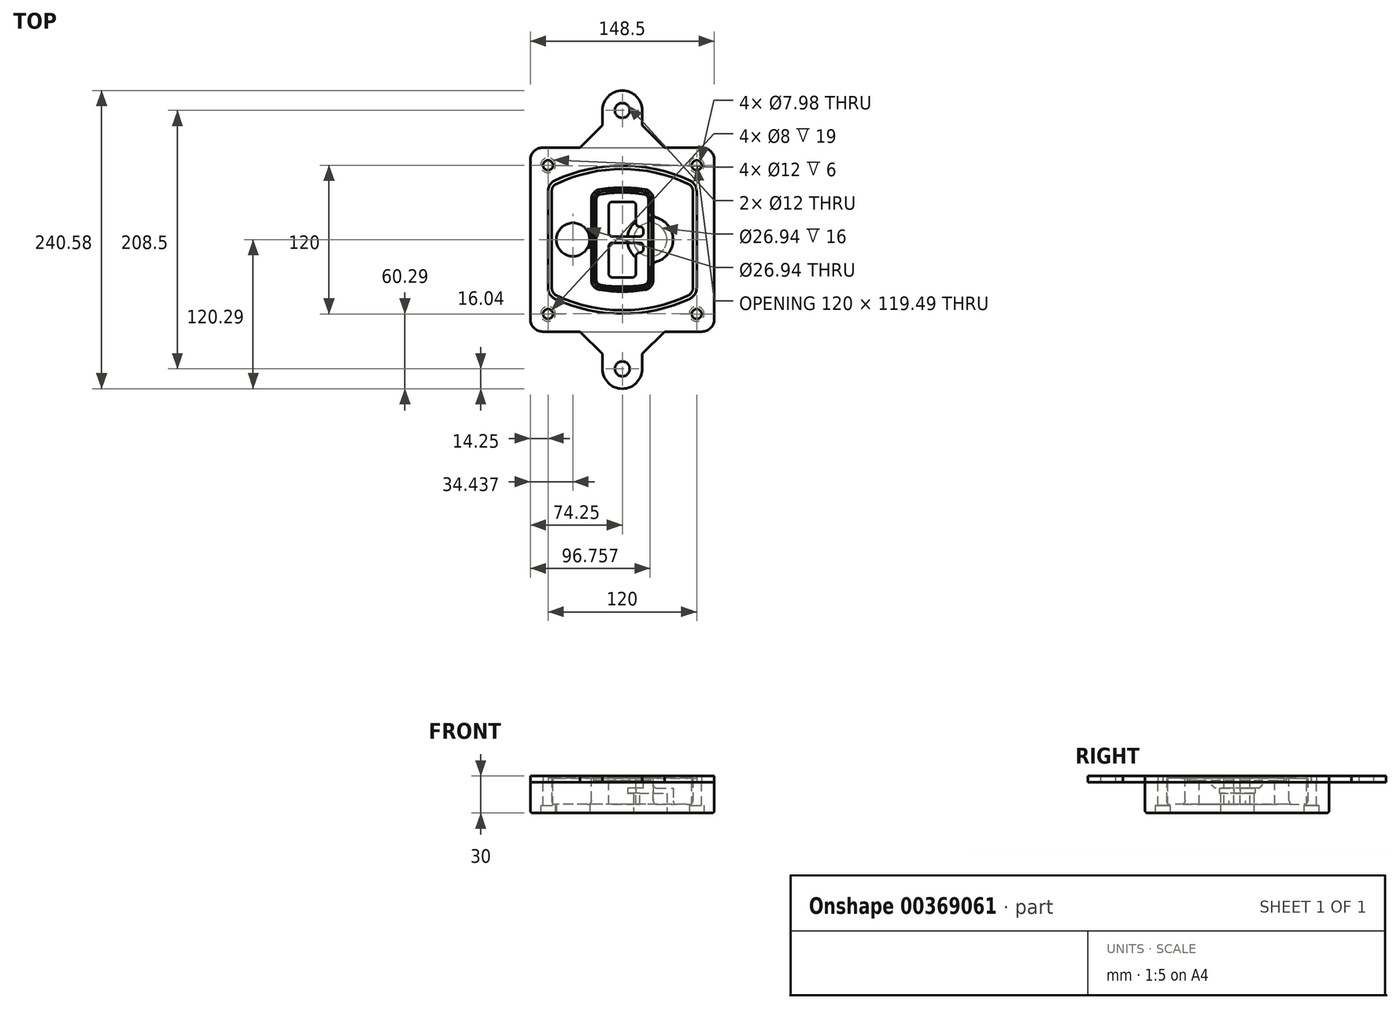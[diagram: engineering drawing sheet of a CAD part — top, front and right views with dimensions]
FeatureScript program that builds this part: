
annotation { "Feature Type Name" : "Feature", "Feature Type Description" : "" }
export const myFeature = defineFeature(function(context is Context, id is Id, definition is map)
    precondition{}
    {
        {
            var Q0;
            Q0=qCreatedBy(makeId("Top.planeOp"),FACE);
            var sketch = newSketch(context, id + "F0", { "sketchPlane" : qUnion([Q0])});
            skPoint(sketch, "E0.rect.middle", {"position": v(0, 0) * mm});
            skLineSegment(sketch, "E1.bottom", {"start": v(-64.25, -74.25) * mm, "end": v(64.25, -74.25) * mm});
            skLineSegment(sketch, "E1.top", {"start": v(-64.25, 74.25) * mm, "end": v(64.25, 74.25) * mm});
            skLineSegment(sketch, "E1.left", {"start": v(-74.25, -64.25) * mm, "end": v(-74.25, 64.25) * mm});
            skLineSegment(sketch, "E1.right", {"start": v(74.25, -64.25) * mm, "end": v(74.25, 64.25) * mm});
            skLineSegment(sketch, "E2", {"start": v(-74.25, 74.25) * mm, "end": v(74.25, -74.25) * mm, "construction": true});
            skLineSegment(sketch, "E3", {"start": v(74.25, 74.25) * mm, "end": v(-74.25, -74.25) * mm, "construction": true});
            skCircle(sketch, "E4", {"center": v(-60, 60) * mm, "radius": 4 * mm});
            skCircle(sketch, "E5", {"center": v(60, 60) * mm, "radius": 4 * mm});
            skCircle(sketch, "E6", {"center": v(60, -60) * mm, "radius": 4 * mm});
            skCircle(sketch, "E7", {"center": v(-60, -60) * mm, "radius": 4 * mm});
            skLineSegment(sketch, "E8", {"start": v(-60, 60) * mm, "end": v(60, 60) * mm, "construction": true});
            skLineSegment(sketch, "E9", {"start": v(60, 60) * mm, "end": v(60, -60) * mm, "construction": true});
            skLineSegment(sketch, "E10", {"start": v(60, -60) * mm, "end": v(-60, -60) * mm, "construction": true});
            skLineSegment(sketch, "E11", {"start": v(-60, -60) * mm, "end": v(-60, 60) * mm, "construction": true});
            skLineSegment(sketch, "E12", {"start": v(-60, 38.83) * mm, "end": v(-60, -38.83) * mm});
            skLineSegment(sketch, "E13", {"start": v(60, 38.83) * mm, "end": v(60, -38.83) * mm});
            skArc(sketch, "E14", {"start": v(54.26, 47.88) * mm, "mid": v(0, 60) * mm, "end": v(-54.26, 47.88) * mm});
            skArc(sketch, "E15", {"start": v(-54.26, -47.88) * mm, "mid": v(0, -60) * mm, "end": v(54.26, -47.88) * mm});
            skLineSegment(sketch, "E16", {"start": v(-60, 0) * mm, "end": v(60, 0) * mm, "construction": true});
            skPoint(sketch, "E17.visualSharp", {"position": v(-60, -45) * mm});
            skArc(sketch, "E17.filletArc", {"start": v(-60, -38.83) * mm, "mid": v(-58.44, -44.2) * mm, "end": v(-54.26, -47.88) * mm});
            skPoint(sketch, "E18.visualSharp", {"position": v(-60, 45) * mm});
            skArc(sketch, "E18.filletArc", {"start": v(-54.26, 47.88) * mm, "mid": v(-58.44, 44.2) * mm, "end": v(-60, 38.83) * mm});
            skPoint(sketch, "E19.visualSharp", {"position": v(60, 45) * mm});
            skArc(sketch, "E19.filletArc", {"start": v(60, 38.83) * mm, "mid": v(58.44, 44.2) * mm, "end": v(54.26, 47.88) * mm});
            skPoint(sketch, "E20.visualSharp", {"position": v(60, -45) * mm});
            skArc(sketch, "E20.filletArc", {"start": v(54.26, -47.88) * mm, "mid": v(58.44, -44.2) * mm, "end": v(60, -38.83) * mm});
            skPoint(sketch, "E21.visualSharp", {"position": v(-74.25, 74.25) * mm});
            skArc(sketch, "E21.filletArc", {"start": v(-64.25, 74.25) * mm, "mid": v(-71.32, 71.32) * mm, "end": v(-74.25, 64.25) * mm});
            skPoint(sketch, "E22.visualSharp", {"position": v(74.25, 74.25) * mm});
            skArc(sketch, "E22.filletArc", {"start": v(74.25, 64.25) * mm, "mid": v(71.32, 71.32) * mm, "end": v(64.25, 74.25) * mm});
            skPoint(sketch, "E23.visualSharp", {"position": v(74.25, -74.25) * mm});
            skArc(sketch, "E23.filletArc", {"start": v(64.25, -74.25) * mm, "mid": v(71.32, -71.32) * mm, "end": v(74.25, -64.25) * mm});
            skPoint(sketch, "E24.visualSharp", {"position": v(-74.25, -74.25) * mm});
            skArc(sketch, "E24.filletArc", {"start": v(-74.25, -64.25) * mm, "mid": v(-71.32, -71.32) * mm, "end": v(-64.25, -74.25) * mm});
            skArc(sketch, "E25.0", {"start": v(57, 38.83) * mm, "mid": v(55.9, 42.58) * mm, "end": v(52.98, 45.17) * mm});
            skLineSegment(sketch, "E25.1", {"start": v(57, 38.83) * mm, "end": v(57, -38.83) * mm});
            skArc(sketch, "E25.2", {"start": v(52.98, -45.17) * mm, "mid": v(55.9, -42.58) * mm, "end": v(57, -38.83) * mm});
            skArc(sketch, "E25.3", {"start": v(-52.98, -45.17) * mm, "mid": v(0, -57) * mm, "end": v(52.98, -45.17) * mm});
            skArc(sketch, "E25.4", {"start": v(-57, -38.83) * mm, "mid": v(-55.9, -42.58) * mm, "end": v(-52.98, -45.17) * mm});
            skArc(sketch, "E25.5", {"start": v(52.98, 45.17) * mm, "mid": v(0, 57) * mm, "end": v(-52.98, 45.17) * mm});
            skLineSegment(sketch, "E25.6", {"start": v(-57, 38.83) * mm, "end": v(-57, -38.83) * mm});
            skArc(sketch, "E25.7", {"start": v(-52.98, 45.17) * mm, "mid": v(-55.9, 42.58) * mm, "end": v(-57, 38.83) * mm});
            skArc(sketch, "E26.0", {"start": v(-55.96, 51.5) * mm, "mid": v(-61.82, 46.33) * mm, "end": v(-64, 38.83) * mm});
            skArc(sketch, "E26.1", {"start": v(55.96, 51.5) * mm, "mid": v(0, 64) * mm, "end": v(-55.96, 51.5) * mm});
            skArc(sketch, "E26.2", {"start": v(64, 38.83) * mm, "mid": v(61.82, 46.33) * mm, "end": v(55.96, 51.5) * mm});
            skLineSegment(sketch, "E26.3", {"start": v(64, 38.83) * mm, "end": v(64, -38.83) * mm});
            skArc(sketch, "E26.4", {"start": v(55.96, -51.5) * mm, "mid": v(61.82, -46.33) * mm, "end": v(64, -38.83) * mm});
            skLineSegment(sketch, "E26.5", {"start": v(-64, 38.83) * mm, "end": v(-64, -38.83) * mm});
            skArc(sketch, "E26.6", {"start": v(-55.96, -51.5) * mm, "mid": v(0, -64) * mm, "end": v(55.96, -51.5) * mm});
            skArc(sketch, "E26.7", {"start": v(-64, -38.83) * mm, "mid": v(-61.82, -46.33) * mm, "end": v(-55.96, -51.5) * mm});
            skSolve(sketch);
        }
        {
            var Q0;
            Q0=makeQuery(id+"F0.imprint","IMPRINT",FACE,{"disambiguationData":[TD([[makeQuery(id+"F0.imprint","IMPRINT",EDGE,{"derivedFrom":sQuery(id+"F0.wireOp",EDGE,"E1.bottom")}),1.0]])]});
            var Q1;
            Q1=makeQuery(id+"F0.imprint","IMPRINT",FACE,{"disambiguationData":[TD([[makeQuery(id+"F0.imprint","IMPRINT",EDGE,{"derivedFrom":sQuery(id+"F0.wireOp",EDGE,"E12")}),1.0]])]});
            var Q2;
            Q2=makeQuery(id+"F0.imprint","IMPRINT",FACE,{"disambiguationData":[TD([[makeQuery(id+"F0.imprint","IMPRINT",EDGE,{"derivedFrom":sQuery(id+"F0.wireOp",EDGE,"E25.0")}),1.0]])]});
            var Q3;
            Q3=makeQuery(id+"F0.imprint","IMPRINT",FACE,{"disambiguationData":[TD([[makeQuery(id+"F0.imprint","IMPRINT",EDGE,{"derivedFrom":sQuery(id+"F0.wireOp",EDGE,"E12")}),-1.0]])]});
            extrude(context, id + "F1", {"entities" : qUnion([Q0, Q1, Q2, Q3]), "oppositeDirection" : true, "depth" : 25 * mm});
        }
        {
            var Q0;
            Q0=makeQuery(id+"F0.imprint","IMPRINT",FACE,{"disambiguationData":[TD([[makeQuery(id+"F0.imprint","IMPRINT",EDGE,{"derivedFrom":sQuery(id+"F0.wireOp",EDGE,"E12")}),1.0]])]});
            extrude(context, id + "F2", {"entities" : qUnion([Q0]), "operationType" : NewBodyOperationType.ADD, "depth" : 3 * mm});
        }
        {
            var Q0;
            Q0=makeQuery(id+"F0.imprint","IMPRINT",FACE,{"disambiguationData":[TD([[makeQuery(id+"F0.imprint","IMPRINT",EDGE,{"derivedFrom":sQuery(id+"F0.wireOp",EDGE,"E25.0")}),1.0]])]});
            extrude(context, id + "F3", {"entities" : qUnion([Q0]), "operationType" : NewBodyOperationType.REMOVE, "oppositeDirection" : true, "depth" : 18 * mm});
        }
        {
            var Q0;
            Q0=makeQuery(id+"F2.opExtrude","CAP_FACE",FACE,{"disambiguationData":[OSD([sQuery(id+"F0.wireOp",EDGE,"E12"),sQuery(id+"F0.wireOp",EDGE,"E13"),sQuery(id+"F0.wireOp",EDGE,"E14"),sQuery(id+"F0.wireOp",EDGE,"E15"),sQuery(id+"F0.wireOp",EDGE,"E17.filletArc"),sQuery(id+"F0.wireOp",EDGE,"E18.filletArc"),sQuery(id+"F0.wireOp",EDGE,"E19.filletArc"),sQuery(id+"F0.wireOp",EDGE,"E20.filletArc"),sQuery(id+"F0.wireOp",EDGE,"E25.0"),sQuery(id+"F0.wireOp",EDGE,"E25.1"),sQuery(id+"F0.wireOp",EDGE,"E25.2"),sQuery(id+"F0.wireOp",EDGE,"E25.3"),sQuery(id+"F0.wireOp",EDGE,"E25.4"),sQuery(id+"F0.wireOp",EDGE,"E25.5"),sQuery(id+"F0.wireOp",EDGE,"E25.6"),sQuery(id+"F0.wireOp",EDGE,"E25.7")])],"isStart":false});
            var sketch = newSketch(context, id + "F4", { "sketchPlane" : qUnion([Q0])});
            skArc(sketch, "E27.0", {"start": v(-18.34, -40.45) * mm, "mid": v(0, -42) * mm, "end": v(18.34, -40.45) * mm});
            skArc(sketch, "E28.0", {"start": v(18.34, 40.45) * mm, "mid": v(0, 42) * mm, "end": v(-18.34, 40.45) * mm});
            skLineSegment(sketch, "E29", {"start": v(-25, 32.57) * mm, "end": v(-25, -32.57) * mm});
            skLineSegment(sketch, "E30", {"start": v(25, 32.57) * mm, "end": v(25, -32.57) * mm});
            skLineSegment(sketch, "E31", {"start": v(-25, 39.1) * mm, "end": v(25, 39.1) * mm, "construction": true});
            skLineSegment(sketch, "E32", {"start": v(-25, -39.1) * mm, "end": v(25, -39.1) * mm, "construction": true});
            skPoint(sketch, "E33.visualSharp", {"position": v(-25, 39.1) * mm});
            skArc(sketch, "E33.filletArc", {"start": v(-18.34, 40.45) * mm, "mid": v(-23.11, 37.73) * mm, "end": v(-25, 32.57) * mm});
            skPoint(sketch, "E34.visualSharp", {"position": v(25, 39.1) * mm});
            skArc(sketch, "E34.filletArc", {"start": v(25, 32.57) * mm, "mid": v(23.11, 37.73) * mm, "end": v(18.34, 40.45) * mm});
            skPoint(sketch, "E35.visualSharp", {"position": v(25, -39.1) * mm});
            skArc(sketch, "E35.filletArc", {"start": v(18.34, -40.45) * mm, "mid": v(23.11, -37.73) * mm, "end": v(25, -32.57) * mm});
            skPoint(sketch, "E36.visualSharp", {"position": v(-25, -39.1) * mm});
            skArc(sketch, "E36.filletArc", {"start": v(-25, -32.57) * mm, "mid": v(-23.11, -37.73) * mm, "end": v(-18.34, -40.45) * mm});
            skArc(sketch, "E37.0", {"start": v(52.98, 45.17) * mm, "mid": v(0, 57) * mm, "end": v(-52.98, 45.17) * mm});
            skArc(sketch, "E37.1", {"start": v(-52.98, 45.17) * mm, "mid": v(-55.9, 42.58) * mm, "end": v(-57, 38.83) * mm});
            skLineSegment(sketch, "E37.2", {"start": v(-57, 38.83) * mm, "end": v(-57, -38.83) * mm});
            skArc(sketch, "E37.3", {"start": v(-57, -38.83) * mm, "mid": v(-55.9, -42.58) * mm, "end": v(-52.98, -45.17) * mm});
            skArc(sketch, "E37.4", {"start": v(-52.98, -45.17) * mm, "mid": v(0, -57) * mm, "end": v(52.98, -45.17) * mm});
            skArc(sketch, "E37.5", {"start": v(52.98, -45.17) * mm, "mid": v(55.9, -42.58) * mm, "end": v(57, -38.83) * mm});
            skLineSegment(sketch, "E37.6", {"start": v(57, 38.83) * mm, "end": v(57, -38.83) * mm});
            skArc(sketch, "E37.7", {"start": v(57, 38.83) * mm, "mid": v(55.9, 42.58) * mm, "end": v(52.98, 45.17) * mm});
            skLineSegment(sketch, "E38.0", {"start": v(23, 32.57) * mm, "end": v(23, -32.57) * mm});
            skArc(sketch, "E38.1", {"start": v(18, -38.48) * mm, "mid": v(21.58, -36.44) * mm, "end": v(23, -32.57) * mm});
            skArc(sketch, "E38.2", {"start": v(-18, -38.48) * mm, "mid": v(0, -40) * mm, "end": v(18, -38.48) * mm});
            skArc(sketch, "E38.3", {"start": v(-23, -32.57) * mm, "mid": v(-21.58, -36.44) * mm, "end": v(-18, -38.48) * mm});
            skLineSegment(sketch, "E38.4", {"start": v(-23, 32.57) * mm, "end": v(-23, -32.57) * mm});
            skArc(sketch, "E38.5", {"start": v(23, 32.57) * mm, "mid": v(21.58, 36.44) * mm, "end": v(18, 38.48) * mm});
            skArc(sketch, "E38.6", {"start": v(-18, 38.48) * mm, "mid": v(-21.58, 36.44) * mm, "end": v(-23, 32.57) * mm});
            skArc(sketch, "E38.7", {"start": v(18, 38.48) * mm, "mid": v(0, 40) * mm, "end": v(-18, 38.48) * mm});
            skArc(sketch, "E39.0", {"start": v(21, 32.57) * mm, "mid": v(20.06, 35.15) * mm, "end": v(17.67, 36.5) * mm});
            skLineSegment(sketch, "E39.1", {"start": v(21, 32.57) * mm, "end": v(21, -32.57) * mm});
            skArc(sketch, "E39.2", {"start": v(17.67, -36.5) * mm, "mid": v(20.06, -35.15) * mm, "end": v(21, -32.57) * mm});
            skArc(sketch, "E39.3", {"start": v(-17.67, -36.5) * mm, "mid": v(0, -38) * mm, "end": v(17.67, -36.5) * mm});
            skArc(sketch, "E39.4", {"start": v(-21, -32.57) * mm, "mid": v(-20.06, -35.15) * mm, "end": v(-17.67, -36.5) * mm});
            skArc(sketch, "E39.5", {"start": v(17.67, 36.5) * mm, "mid": v(0, 38) * mm, "end": v(-17.67, 36.5) * mm});
            skLineSegment(sketch, "E39.6", {"start": v(-21, 32.57) * mm, "end": v(-21, -32.57) * mm});
            skArc(sketch, "E39.7", {"start": v(-17.67, 36.5) * mm, "mid": v(-20.06, 35.15) * mm, "end": v(-21, 32.57) * mm});
            skLineSegment(sketch, "E40", {"start": v(-25, 0) * mm, "end": v(25, 0) * mm, "construction": true});
            skLineSegment(sketch, "E41", {"start": v(-11, 5.5) * mm, "end": v(-11, 27.5) * mm});
            skLineSegment(sketch, "E42", {"start": v(-8, 30.5) * mm, "end": v(8, 30.5) * mm});
            skLineSegment(sketch, "E43", {"start": v(11, 27.5) * mm, "end": v(11, 13.5) * mm});
            skLineSegment(sketch, "E44", {"start": v(14, 10.5) * mm, "end": v(14, 10.5) * mm});
            skLineSegment(sketch, "E45", {"start": v(17, 7.5) * mm, "end": v(17, 5.5) * mm});
            skLineSegment(sketch, "E46", {"start": v(14, 2.5) * mm, "end": v(-8, 2.5) * mm});
            skPoint(sketch, "E47.visualSharp", {"position": v(-11, 30.5) * mm});
            skArc(sketch, "E47.filletArc", {"start": v(-8, 30.5) * mm, "mid": v(-10.12, 29.62) * mm, "end": v(-11, 27.5) * mm});
            skPoint(sketch, "E48.visualSharp", {"position": v(11, 30.5) * mm});
            skArc(sketch, "E48.filletArc", {"start": v(11, 27.5) * mm, "mid": v(10.12, 29.62) * mm, "end": v(8, 30.5) * mm});
            skPoint(sketch, "E49.visualSharp", {"position": v(11, 10.5) * mm});
            skArc(sketch, "E49.filletArc", {"start": v(11, 13.5) * mm, "mid": v(11.88, 11.38) * mm, "end": v(14, 10.5) * mm});
            skPoint(sketch, "E50.visualSharp", {"position": v(17, 10.5) * mm});
            skArc(sketch, "E50.filletArc", {"start": v(17, 7.5) * mm, "mid": v(16.12, 9.62) * mm, "end": v(14, 10.5) * mm});
            skPoint(sketch, "E51.visualSharp", {"position": v(17, 2.5) * mm});
            skArc(sketch, "E51.filletArc", {"start": v(14, 2.5) * mm, "mid": v(16.12, 3.38) * mm, "end": v(17, 5.5) * mm});
            skPoint(sketch, "E52.visualSharp", {"position": v(-11, 2.5) * mm});
            skArc(sketch, "E52.filletArc", {"start": v(-11, 5.5) * mm, "mid": v(-10.12, 3.38) * mm, "end": v(-8, 2.5) * mm});
            skLineSegment(sketch, "E53.0.MirrorCS", {"start": v(14, -2.5) * mm, "end": v(-8, -2.5) * mm});
            skArc(sketch, "E54.0.MirrorCS", {"start": v(-11, -5.5) * mm, "mid": v(-10.12, -3.38) * mm, "end": v(-8, -2.5) * mm});
            skLineSegment(sketch, "E55.0.MirrorCS", {"start": v(-11, -5.5) * mm, "end": v(-11, -27.5) * mm});
            skArc(sketch, "E56.0.MirrorCS", {"start": v(-8, -30.5) * mm, "mid": v(-10.12, -29.62) * mm, "end": v(-11, -27.5) * mm});
            skLineSegment(sketch, "E57.0.MirrorCS", {"start": v(-8, -30.5) * mm, "end": v(8, -30.5) * mm});
            skArc(sketch, "E58.0.MirrorCS", {"start": v(11, -27.5) * mm, "mid": v(10.12, -29.62) * mm, "end": v(8, -30.5) * mm});
            skLineSegment(sketch, "E59.0.MirrorCS", {"start": v(11, -27.5) * mm, "end": v(11, -13.5) * mm});
            skArc(sketch, "E60.0.MirrorCS", {"start": v(11, -13.5) * mm, "mid": v(11.88, -11.38) * mm, "end": v(14, -10.5) * mm});
            skArc(sketch, "E61.0.MirrorCS", {"start": v(17, -7.5) * mm, "mid": v(16.12, -9.62) * mm, "end": v(14, -10.5) * mm});
            skLineSegment(sketch, "E62.0.MirrorCS", {"start": v(17, -7.5) * mm, "end": v(17, -5.5) * mm});
            skArc(sketch, "E63.0.MirrorCS", {"start": v(14, -2.5) * mm, "mid": v(16.12, -3.38) * mm, "end": v(17, -5.5) * mm});
            skSolve(sketch);
        }
        {
            var Q0;
            Q0=makeQuery(id+"F4.imprint","IMPRINT",FACE,{"disambiguationData":[TD([[makeQuery(id+"F4.imprint","IMPRINT",EDGE,{"derivedFrom":sQuery(id+"F4.wireOp",EDGE,"E27.0")}),1.0]])]});
            var Q1;
            Q1=makeQuery(id+"F4.imprint","IMPRINT",FACE,{"disambiguationData":[TD([[makeQuery(id+"F4.imprint","IMPRINT",EDGE,{"derivedFrom":sQuery(id+"F4.wireOp",EDGE,"E38.0")}),-1.0]])]});
            var Q2;
            Q2=makeQuery(id+"F4.imprint","IMPRINT",FACE,{"disambiguationData":[TD([[makeQuery(id+"F4.imprint","IMPRINT",EDGE,{"derivedFrom":sQuery(id+"F4.wireOp",EDGE,"E39.0")}),1.0]])]});
            extrude(context, id + "F5", {"entities" : qUnion([Q0, Q1, Q2]), "operationType" : NewBodyOperationType.ADD, "endBound" : BoundingType.UP_TO_NEXT, "oppositeDirection" : true, "depth" : 25 * mm});
        }
        {
            var Q0;
            Q0=makeQuery(id+"F4.imprint","IMPRINT",FACE,{"disambiguationData":[TD([[makeQuery(id+"F4.imprint","IMPRINT",EDGE,{"derivedFrom":sQuery(id+"F4.wireOp",EDGE,"E38.0")}),-1.0]])]});
            extrude(context, id + "F6", {"entities" : qUnion([Q0]), "operationType" : NewBodyOperationType.REMOVE, "oppositeDirection" : true, "depth" : 2 * mm});
        }
        {
            var Q0;
            Q0=makeQuery(id+"F1.opExtrude","CAP_FACE",FACE,{"disambiguationData":[OSD([sQuery(id+"F0.wireOp",EDGE,"E1.bottom"),sQuery(id+"F0.wireOp",EDGE,"E1.top"),sQuery(id+"F0.wireOp",EDGE,"E1.left"),sQuery(id+"F0.wireOp",EDGE,"E1.right"),sQuery(id+"F0.wireOp",EDGE,"E4"),sQuery(id+"F0.wireOp",EDGE,"E5"),sQuery(id+"F0.wireOp",EDGE,"E6"),sQuery(id+"F0.wireOp",EDGE,"E7"),sQuery(id+"F0.wireOp",EDGE,"E21.filletArc"),sQuery(id+"F0.wireOp",EDGE,"E22.filletArc"),sQuery(id+"F0.wireOp",EDGE,"E23.filletArc"),sQuery(id+"F0.wireOp",EDGE,"E24.filletArc")])],"isStart":false});
            var sketch = newSketch(context, id + "F7", { "sketchPlane" : qUnion([Q0])});
            skCircle(sketch, "E64", {"center": v(22.5, 0) * mm, "radius": 13.47 * mm});
            skCircle(sketch, "E65", {"center": v(-39.81, 0) * mm, "radius": 13.47 * mm});
            skLineSegment(sketch, "E66", {"start": v(74.25, 0) * mm, "end": v(-74.25, 0) * mm});
            skCircle(sketch, "E67", {"center": v(22.5, 0) * mm, "radius": 18.47 * mm});
            skCircle(sketch, "E68", {"center": v(60, -60) * mm, "radius": 6 * mm});
            skCircle(sketch, "E69", {"center": v(-60, -60) * mm, "radius": 6 * mm});
            skCircle(sketch, "E70", {"center": v(-60, 60) * mm, "radius": 6 * mm});
            skCircle(sketch, "E71", {"center": v(60, 60) * mm, "radius": 6 * mm});
            skSolve(sketch);
        }
        {
            var Q0;
            {var subQ1=sQuery(id+"F7.wireOp",EDGE,"E66");var subQ4=sQuery(id+"F7.wireOp",EDGE,"E64");var subQ6=makeQuery(id+"F7.imprint","INTERSECT",VERTEX,{"disambiguationData":[OD(0.0)],"derivedFrom":[subQ4,subQ1]});Q0=makeQuery(id+"F7.imprint","IMPRINT",FACE,{"disambiguationData":[TD([[makeQuery(id+"F7.imprint","IMPRINT",EDGE,{"disambiguationData":[TD([[subQ6,-1.0]])],"derivedFrom":subQ4}),-1.0]])]});}
            var Q1;
            {var subQ0=sQuery(id+"F7.wireOp",EDGE,"E66");var subQ1=sQuery(id+"F7.wireOp",EDGE,"E64");var subQ3=makeQuery(id+"F7.imprint","INTERSECT",VERTEX,{"disambiguationData":[OD(0.0)],"derivedFrom":[subQ1,subQ0]});Q1=makeQuery(id+"F7.imprint","IMPRINT",FACE,{"disambiguationData":[TD([[makeQuery(id+"F7.imprint","IMPRINT",EDGE,{"disambiguationData":[TD([[subQ3,-1.0]])],"derivedFrom":subQ1}),1.0]])]});}
            var Q2;
            {var subQ0=sQuery(id+"F7.wireOp",EDGE,"E66");var subQ1=sQuery(id+"F7.wireOp",EDGE,"E64");var subQ3=makeQuery(id+"F7.imprint","INTERSECT",VERTEX,{"disambiguationData":[OD(0.0)],"derivedFrom":[subQ1,subQ0]});Q2=makeQuery(id+"F7.imprint","IMPRINT",FACE,{"disambiguationData":[TD([[makeQuery(id+"F7.imprint","IMPRINT",EDGE,{"disambiguationData":[TD([[subQ3,1.0]])],"derivedFrom":subQ1}),1.0]])]});}
            var Q3;
            {var subQ1=sQuery(id+"F7.wireOp",EDGE,"E66");var subQ4=sQuery(id+"F7.wireOp",EDGE,"E64");var subQ6=makeQuery(id+"F7.imprint","INTERSECT",VERTEX,{"disambiguationData":[OD(0.0)],"derivedFrom":[subQ4,subQ1]});Q3=makeQuery(id+"F7.imprint","IMPRINT",FACE,{"disambiguationData":[TD([[makeQuery(id+"F7.imprint","IMPRINT",EDGE,{"disambiguationData":[TD([[subQ6,1.0]])],"derivedFrom":subQ4}),-1.0]])]});}
            extrude(context, id + "F8", {"entities" : qUnion([Q0, Q1, Q2, Q3]), "operationType" : NewBodyOperationType.ADD, "oppositeDirection" : true, "depth" : 20 * mm});
        }
        {
            var Q0;
            {var subQ0=sQuery(id+"F7.wireOp",EDGE,"E66");var subQ1=sQuery(id+"F7.wireOp",EDGE,"E64");var subQ3=makeQuery(id+"F7.imprint","INTERSECT",VERTEX,{"disambiguationData":[OD(0.0)],"derivedFrom":[subQ1,subQ0]});Q0=makeQuery(id+"F7.imprint","IMPRINT",FACE,{"disambiguationData":[TD([[makeQuery(id+"F7.imprint","IMPRINT",EDGE,{"disambiguationData":[TD([[subQ3,-1.0]])],"derivedFrom":subQ1}),1.0]])]});}
            var Q1;
            {var subQ0=sQuery(id+"F7.wireOp",EDGE,"E66");var subQ1=sQuery(id+"F7.wireOp",EDGE,"E64");var subQ3=makeQuery(id+"F7.imprint","INTERSECT",VERTEX,{"disambiguationData":[OD(0.0)],"derivedFrom":[subQ1,subQ0]});Q1=makeQuery(id+"F7.imprint","IMPRINT",FACE,{"disambiguationData":[TD([[makeQuery(id+"F7.imprint","IMPRINT",EDGE,{"disambiguationData":[TD([[subQ3,1.0]])],"derivedFrom":subQ1}),1.0]])]});}
            extrude(context, id + "F9", {"entities" : qUnion([Q0, Q1]), "operationType" : NewBodyOperationType.REMOVE, "oppositeDirection" : true, "depth" : 16 * mm});
        }
        {
            var Q0;
            {var subQ0=sQuery(id+"F7.wireOp",EDGE,"E66");var subQ1=sQuery(id+"F7.wireOp",EDGE,"E65");var subQ3=makeQuery(id+"F7.imprint","INTERSECT",VERTEX,{"disambiguationData":[OD(0.0)],"derivedFrom":[subQ1,subQ0]});Q0=makeQuery(id+"F7.imprint","IMPRINT",FACE,{"disambiguationData":[TD([[makeQuery(id+"F7.imprint","IMPRINT",EDGE,{"disambiguationData":[TD([[subQ3,-1.0]])],"derivedFrom":subQ1}),1.0]])]});}
            var Q1;
            {var subQ0=sQuery(id+"F7.wireOp",EDGE,"E66");var subQ1=sQuery(id+"F7.wireOp",EDGE,"E65");var subQ3=makeQuery(id+"F7.imprint","INTERSECT",VERTEX,{"disambiguationData":[OD(0.0)],"derivedFrom":[subQ1,subQ0]});Q1=makeQuery(id+"F7.imprint","IMPRINT",FACE,{"disambiguationData":[TD([[makeQuery(id+"F7.imprint","IMPRINT",EDGE,{"disambiguationData":[TD([[subQ3,1.0]])],"derivedFrom":subQ1}),1.0]])]});}
            extrude(context, id + "F10", {"entities" : qUnion([Q0, Q1]), "operationType" : NewBodyOperationType.REMOVE, "oppositeDirection" : true, "depth" : 25 * mm});
        }
        {
            var Q0;
            Q0=makeQuery(id+"F7.imprint","IMPRINT",FACE,{"disambiguationData":[TD([[makeQuery(id+"F7.imprint","IMPRINT",EDGE,{"derivedFrom":sQuery(id+"F7.wireOp",EDGE,"E68")}),1.0]])]});
            var Q1;
            Q1=makeQuery(id+"F7.imprint","IMPRINT",FACE,{"disambiguationData":[TD([[makeQuery(id+"F7.imprint","IMPRINT",EDGE,{"derivedFrom":makeQuery(id+"F1.opExtrude","CAP_EDGE",EDGE,{"disambiguationData":[OSD([sQuery(id+"F0.wireOp",EDGE,"E5")])],"isStart":false})}),-1.0]])]});
            var Q2;
            Q2=makeQuery(id+"F7.imprint","IMPRINT",FACE,{"disambiguationData":[TD([[makeQuery(id+"F7.imprint","IMPRINT",EDGE,{"derivedFrom":sQuery(id+"F7.wireOp",EDGE,"E69")}),1.0]])]});
            var Q3;
            Q3=makeQuery(id+"F7.imprint","IMPRINT",FACE,{"disambiguationData":[TD([[makeQuery(id+"F7.imprint","IMPRINT",EDGE,{"derivedFrom":makeQuery(id+"F1.opExtrude","CAP_EDGE",EDGE,{"disambiguationData":[OSD([sQuery(id+"F0.wireOp",EDGE,"E4")])],"isStart":false})}),-1.0]])]});
            var Q4;
            Q4=makeQuery(id+"F7.imprint","IMPRINT",FACE,{"disambiguationData":[TD([[makeQuery(id+"F7.imprint","IMPRINT",EDGE,{"derivedFrom":sQuery(id+"F7.wireOp",EDGE,"E70")}),1.0]])]});
            var Q5;
            Q5=makeQuery(id+"F7.imprint","IMPRINT",FACE,{"disambiguationData":[TD([[makeQuery(id+"F7.imprint","IMPRINT",EDGE,{"derivedFrom":makeQuery(id+"F1.opExtrude","CAP_EDGE",EDGE,{"disambiguationData":[OSD([sQuery(id+"F0.wireOp",EDGE,"E7")])],"isStart":false})}),-1.0]])]});
            var Q6;
            Q6=makeQuery(id+"F7.imprint","IMPRINT",FACE,{"disambiguationData":[TD([[makeQuery(id+"F7.imprint","IMPRINT",EDGE,{"derivedFrom":sQuery(id+"F7.wireOp",EDGE,"E71")}),1.0]])]});
            var Q7;
            Q7=makeQuery(id+"F7.imprint","IMPRINT",FACE,{"disambiguationData":[TD([[makeQuery(id+"F7.imprint","IMPRINT",EDGE,{"derivedFrom":makeQuery(id+"F1.opExtrude","CAP_EDGE",EDGE,{"disambiguationData":[OSD([sQuery(id+"F0.wireOp",EDGE,"E6")])],"isStart":false})}),-1.0]])]});
            extrude(context, id + "F11", {"entities" : qUnion([Q0, Q1, Q2, Q3, Q4, Q5, Q6, Q7]), "operationType" : NewBodyOperationType.REMOVE, "oppositeDirection" : true, "depth" : 6 * mm});
        }
        {
            var Q0;
            Q0=makeQuery(id+"F9.boolean.opBoolean","COPY",FACE,{"derivedFrom":makeQuery(id+"F9.opExtrude","CAP_FACE",FACE,{"disambiguationData":[OSD([sQuery(id+"F7.wireOp",EDGE,"E64")])],"isStart":false})});
            var sketch = newSketch(context, id + "F12", { "sketchPlane" : qUnion([Q0])});
            skArc(sketch, "E72.0", {"start": v(11, 14.45) * mm, "mid": v(6.45, 9.13) * mm, "end": v(4.2, 2.5) * mm});
            skArc(sketch, "E72.1", {"start": v(4.2, -2.5) * mm, "mid": v(6.45, -9.13) * mm, "end": v(11, -14.45) * mm});
            skLineSegment(sketch, "E73", {"start": v(4.2, -2.5) * mm, "end": v(14, -2.5) * mm});
            skLineSegment(sketch, "E74.0", {"start": v(14, 2.5) * mm, "end": v(4.2, 2.5) * mm});
            skArc(sketch, "E74.1", {"start": v(14, 2.5) * mm, "mid": v(16.12, 3.38) * mm, "end": v(17, 5.5) * mm});
            skLineSegment(sketch, "E74.2", {"start": v(17, 7.5) * mm, "end": v(17, 5.5) * mm});
            skArc(sketch, "E74.3", {"start": v(17, 7.5) * mm, "mid": v(16.12, 9.62) * mm, "end": v(14, 10.5) * mm});
            skArc(sketch, "E74.4", {"start": v(11, 13.5) * mm, "mid": v(11.88, 11.38) * mm, "end": v(14, 10.5) * mm});
            skLineSegment(sketch, "E74.5", {"start": v(11, 14.45) * mm, "end": v(11, 13.5) * mm});
            skLineSegment(sketch, "E74.7", {"start": v(14, -2.5) * mm, "end": v(4.2, -2.5) * mm});
            skArc(sketch, "E74.8", {"start": v(14, -2.5) * mm, "mid": v(16.12, -3.38) * mm, "end": v(17, -5.5) * mm});
            skLineSegment(sketch, "E74.9", {"start": v(17, -7.5) * mm, "end": v(17, -5.5) * mm});
            skArc(sketch, "E74.10", {"start": v(17, -7.5) * mm, "mid": v(16.12, -9.62) * mm, "end": v(14, -10.5) * mm});
            skArc(sketch, "E74.11", {"start": v(11, -13.5) * mm, "mid": v(11.88, -11.38) * mm, "end": v(14, -10.5) * mm});
            skLineSegment(sketch, "E74.12", {"start": v(11, -14.45) * mm, "end": v(11, -13.5) * mm});
            skPoint(sketch, "E75.orphan", {"position": v(11, -27.5) * mm});
            skPoint(sketch, "E76.orphan", {"position": v(-8, -2.5) * mm});
            skPoint(sketch, "E77.orphan", {"position": v(-8, 2.5) * mm});
            skPoint(sketch, "E78.orphan", {"position": v(11, 27.5) * mm});
            skSolve(sketch);
        }
        {
            var Q0;
            {var subQ7=sQuery(id+"F12.wireOp",EDGE,"E72.0");var subQ14=sQuery(id+"F12.wireOp",EDGE,"E72.1");var subQ16=sQuery(id+"F12.wireOp",EDGE,"E74.1");var subQ18=sQuery(id+"F12.wireOp",EDGE,"E74.8");Q0=qUnion([makeQuery(id+"F12.imprint","IMPRINT",FACE,{"disambiguationData":[TD([[makeQuery(id+"F12.imprint","IMPRINT",EDGE,{"derivedFrom":subQ7}),1.0]])]}),makeQuery(id+"F12.imprint","IMPRINT",FACE,{"disambiguationData":[TD([[makeQuery(id+"F12.imprint","IMPRINT",EDGE,{"derivedFrom":subQ14}),1.0]])]}),makeQuery(id+"F12.imprint","IMPRINT",FACE,{"disambiguationData":[TD([[makeQuery(id+"F12.imprint","IMPRINT",EDGE,{"derivedFrom":subQ16}),1.0]])]}),makeQuery(id+"F12.imprint","IMPRINT",FACE,{"disambiguationData":[TD([[makeQuery(id+"F12.imprint","IMPRINT",EDGE,{"derivedFrom":subQ18}),-1.0]])]})]);}
            var Q1;
            Q1=makeQuery(id+"F5.boolean.opBoolean","SPLIT",FACE,{"disambiguationData":[TD([makeQuery(id+"F5.opExtrude","SWEPT_FACE",FACE,{"disambiguationData":[OSD([sQuery(id+"F4.wireOp",EDGE,"E41")])]})])],"derivedFrom":makeQuery(id+"F3.boolean.opBoolean","COPY",FACE,{"derivedFrom":makeQuery(id+"F3.opExtrude","CAP_FACE",FACE,{"disambiguationData":[OSD([sQuery(id+"F0.wireOp",EDGE,"E25.0"),sQuery(id+"F0.wireOp",EDGE,"E25.1"),sQuery(id+"F0.wireOp",EDGE,"E25.2"),sQuery(id+"F0.wireOp",EDGE,"E25.3"),sQuery(id+"F0.wireOp",EDGE,"E25.4"),sQuery(id+"F0.wireOp",EDGE,"E25.5"),sQuery(id+"F0.wireOp",EDGE,"E25.6"),sQuery(id+"F0.wireOp",EDGE,"E25.7")])],"isStart":false})})});
            extrude(context, id + "F13", {"entities" : qUnion([Q0]), "operationType" : NewBodyOperationType.REMOVE, "endBound" : BoundingType.UP_TO_SURFACE, "endBoundEntityFace" : qUnion([Q1]), "depth" : 25 * mm});
        }
        {
            var Q0;
            Q0=makeQuery(id+"F3.boolean.opBoolean","COPY",EDGE,{"derivedFrom":makeQuery(id+"F3.opExtrude","CAP_EDGE",EDGE,{"disambiguationData":[OSD([sQuery(id+"F0.wireOp",EDGE,"E25.6")])],"isStart":false})});
            var Q1;
            Q1=makeQuery(id+"F8.boolean.opBoolean","INTERSECT",EDGE,{"derivedFrom":[makeQuery(id+"F5.opExtrude","SWEPT_FACE",FACE,{"disambiguationData":[OSD([sQuery(id+"F4.wireOp",EDGE,"E30")])]}),makeQuery(id+"F8.opExtrude","CAP_FACE",FACE,{"disambiguationData":[OSD([sQuery(id+"F7.wireOp",EDGE,"E67")])],"isStart":false})]});
            var Q2;
            Q2=makeQuery(id+"F8.boolean.opBoolean","INTERSECT",EDGE,{"disambiguationData":[OD(1.0)],"derivedFrom":[makeQuery(id+"F5.opExtrude","SWEPT_FACE",FACE,{"disambiguationData":[OSD([sQuery(id+"F4.wireOp",EDGE,"E30")])]}),makeQuery(id+"F8.opExtrude","SWEPT_FACE",FACE,{"disambiguationData":[OSD([sQuery(id+"F7.wireOp",EDGE,"E67")])]})]});
            var Q3;
            {var subQ0=sQuery(id+"F4.wireOp",EDGE,"E30");Q3=makeQuery(id+"F8.boolean.opBoolean","SPLIT",EDGE,{"disambiguationData":[TD([makeQuery(id+"F5.opExtrude","SWEPT_FACE",FACE,{"disambiguationData":[OSD([sQuery(id+"F4.wireOp",EDGE,"E35.filletArc")])]})])],"derivedFrom":makeQuery(id+"F5.opExtrude","CAP_EDGE",EDGE,{"disambiguationData":[OSD([subQ0])],"isStart":false})});}
            var Q4;
            {var subQ0=sQuery(id+"F0.wireOp",EDGE,"E25.7");var subQ1=sQuery(id+"F0.wireOp",EDGE,"E25.1");var subQ2=sQuery(id+"F0.wireOp",EDGE,"E25.6");var subQ3=sQuery(id+"F0.wireOp",EDGE,"E25.5");var subQ4=sQuery(id+"F0.wireOp",EDGE,"E25.4");var subQ5=sQuery(id+"F0.wireOp",EDGE,"E25.0");var subQ6=sQuery(id+"F0.wireOp",EDGE,"E25.2");var subQ7=sQuery(id+"F0.wireOp",EDGE,"E25.3");Q4=makeQuery(id+"F8.boolean.opBoolean","INTERSECT",EDGE,{"derivedFrom":[makeQuery(id+"F5.boolean.opBoolean","SPLIT",FACE,{"disambiguationData":[TD([makeQuery(id+"F2.opExtrude","SWEPT_FACE",FACE,{"disambiguationData":[OSD([subQ5])]})])],"derivedFrom":makeQuery(id+"F3.boolean.opBoolean","COPY",FACE,{"derivedFrom":makeQuery(id+"F3.opExtrude","CAP_FACE",FACE,{"disambiguationData":[OSD([subQ5,subQ1,subQ6,subQ7,subQ4,subQ3,subQ2,subQ0])],"isStart":false})})}),makeQuery(id+"F8.opExtrude","SWEPT_FACE",FACE,{"disambiguationData":[OSD([sQuery(id+"F7.wireOp",EDGE,"E67")])]})]});}
            var Q5;
            Q5=makeQuery(id+"F8.boolean.opBoolean","INTERSECT",EDGE,{"disambiguationData":[OD(0.0)],"derivedFrom":[makeQuery(id+"F5.opExtrude","SWEPT_FACE",FACE,{"disambiguationData":[OSD([sQuery(id+"F4.wireOp",EDGE,"E30")])]}),makeQuery(id+"F8.opExtrude","SWEPT_FACE",FACE,{"disambiguationData":[OSD([sQuery(id+"F7.wireOp",EDGE,"E67")])]})]});
            fillet(context, id + "F14", {"entities" : qUnion([Q0, Q1, Q2, Q3, Q4, Q5]), "radius" : 3 * mm, "tangentPropagation" : true, "allowEdgeOverflow" : false});
        }
        {
            var Q0;
            Q0=makeQuery(id+"F1.opExtrude","CAP_EDGE",EDGE,{"disambiguationData":[OSD([sQuery(id+"F0.wireOp",EDGE,"E1.bottom")])],"isStart":false});
            fillet(context, id + "F15", {"entities" : qUnion([Q0]), "radius" : 2 * mm, "tangentPropagation" : true, "allowEdgeOverflow" : false});
        }
        {
            var Q0;
            {var subQ0=sQuery(id+"F0.wireOp",EDGE,"E21.filletArc");var subQ1=sQuery(id+"F0.wireOp",EDGE,"E7");var subQ2=sQuery(id+"F0.wireOp",EDGE,"E6");var subQ3=sQuery(id+"F0.wireOp",EDGE,"E5");var subQ4=sQuery(id+"F0.wireOp",EDGE,"E4");var subQ5=sQuery(id+"F0.wireOp",EDGE,"E22.filletArc");var subQ6=sQuery(id+"F0.wireOp",EDGE,"E1.bottom");var subQ7=sQuery(id+"F0.wireOp",EDGE,"E1.right");var subQ8=sQuery(id+"F0.wireOp",EDGE,"E1.top");var subQ9=sQuery(id+"F0.wireOp",EDGE,"E1.left");var subQ10=sQuery(id+"F0.wireOp",EDGE,"E23.filletArc");var subQ11=sQuery(id+"F0.wireOp",EDGE,"E24.filletArc");Q0=makeQuery(id+"F2.boolean.opBoolean","SPLIT",FACE,{"disambiguationData":[TD([makeQuery(id+"F1.opExtrude","SWEPT_FACE",FACE,{"disambiguationData":[OSD([subQ6])]})])],"derivedFrom":makeQuery(id+"F1.opExtrude","CAP_FACE",FACE,{"disambiguationData":[OSD([subQ6,subQ8,subQ9,subQ7,subQ4,subQ3,subQ2,subQ1,subQ0,subQ5,subQ10,subQ11])],"isStart":true})});}
            var sketch = newSketch(context, id + "F16", { "sketchPlane" : qUnion([Q0])});
            skCircle(sketch, "E79", {"center": v(0, 104.25) * mm, "radius": 6 * mm});
            skLineSegment(sketch, "E80", {"start": v(-34.04, 74.25) * mm, "end": v(-16.04, 92.25) * mm});
            skLineSegment(sketch, "E81", {"start": v(-16.04, 92.25) * mm, "end": v(-16.04, 104.25) * mm});
            skLineSegment(sketch, "E82", {"start": v(34.04, 74.25) * mm, "end": v(16.04, 92.25) * mm});
            skPoint(sketch, "E83", {"position": v(-21.53, 74.25) * mm});
            skLineSegment(sketch, "E84", {"start": v(16.04, 92.25) * mm, "end": v(16.04, 104.25) * mm});
            skArc(sketch, "E85", {"start": v(16.04, 104.25) * mm, "mid": v(0, 120.29) * mm, "end": v(-16.04, 104.25) * mm});
            skLineSegment(sketch, "E86.MirrorCS", {"start": v(-34.04, -74.25) * mm, "end": v(-16.04, -92.25) * mm});
            skLineSegment(sketch, "E87.MirrorCS", {"start": v(34.04, -74.25) * mm, "end": v(16.04, -92.25) * mm});
            skLineSegment(sketch, "E88.MirrorCS", {"start": v(16.04, -92.25) * mm, "end": v(16.04, -104.25) * mm});
            skLineSegment(sketch, "E89.MirrorCS", {"start": v(-16.04, -92.25) * mm, "end": v(-16.04, -104.25) * mm});
            skArc(sketch, "E90.MirrorCS", {"start": v(16.04, -104.25) * mm, "mid": v(0, -120.29) * mm, "end": v(-16.04, -104.25) * mm});
            skCircle(sketch, "E91.MirrorC", {"center": v(0, -104.25) * mm, "radius": 6 * mm});
            skLineSegment(sketch, "E92", {"start": v(-34.04, 74.25) * mm, "end": v(-64.25, 74.25) * mm});
            skLineSegment(sketch, "E93", {"start": v(-74.25, 64.25) * mm, "end": v(-74.25, -64.25) * mm});
            skLineSegment(sketch, "E94", {"start": v(-34.04, -74.25) * mm, "end": v(-64.25, -74.25) * mm});
            skLineSegment(sketch, "E95", {"start": v(34.04, -74.25) * mm, "end": v(64.25, -74.25) * mm});
            skLineSegment(sketch, "E96", {"start": v(74.25, -64.25) * mm, "end": v(74.25, 64.25) * mm});
            skLineSegment(sketch, "E97", {"start": v(34.04, 74.25) * mm, "end": v(64.25, 74.25) * mm});
            skArc(sketch, "E98", {"start": v(74.25, 64.25) * mm, "mid": v(71.32, 71.32) * mm, "end": v(64.25, 74.25) * mm});
            skArc(sketch, "E99", {"start": v(64.25, -74.25) * mm, "mid": v(71.32, -71.32) * mm, "end": v(74.25, -64.25) * mm});
            skArc(sketch, "E100", {"start": v(-74.25, -64.25) * mm, "mid": v(-71.32, -71.32) * mm, "end": v(-64.25, -74.25) * mm});
            skArc(sketch, "E101", {"start": v(-64.25, 74.25) * mm, "mid": v(-71.32, 71.32) * mm, "end": v(-74.25, 64.25) * mm});
            skCircle(sketch, "E102", {"center": v(-60, 60) * mm, "radius": 3.99 * mm});
            skCircle(sketch, "E103", {"center": v(60, 60) * mm, "radius": 3.99 * mm});
            skCircle(sketch, "E104", {"center": v(60, -60) * mm, "radius": 3.99 * mm});
            skCircle(sketch, "E105", {"center": v(-60, -60) * mm, "radius": 3.99 * mm});
            skLineSegment(sketch, "E106", {"start": v(-60, 38.83) * mm, "end": v(-60, -38.83) * mm});
            skLineSegment(sketch, "E107", {"start": v(60, -38.83) * mm, "end": v(60, 38.83) * mm});
            skArc(sketch, "E108", {"start": v(-54.26, 47.88) * mm, "mid": v(-58.44, 44.2) * mm, "end": v(-60, 38.83) * mm});
            skArc(sketch, "E109", {"start": v(54.26, -47.88) * mm, "mid": v(58.44, -44.2) * mm, "end": v(60, -38.83) * mm});
            skArc(sketch, "E110", {"start": v(60, 38.83) * mm, "mid": v(58.44, 44.2) * mm, "end": v(54.26, 47.88) * mm});
            skArc(sketch, "E111", {"start": v(-60, -38.83) * mm, "mid": v(-58.44, -44.2) * mm, "end": v(-54.26, -47.88) * mm});
            skArc(sketch, "E112", {"start": v(54.26, 47.88) * mm, "mid": v(0, 59.74) * mm, "end": v(-54.26, 47.88) * mm});
            skArc(sketch, "E113", {"start": v(-54.26, -47.88) * mm, "mid": v(0, -59.74) * mm, "end": v(54.26, -47.88) * mm});
            skSolve(sketch);
        }
        {
            var Q0;
            Q0 = qSketchRegion(id + "F16", true);
            extrude(context, id + "F17", {"entities" : qUnion([Q0]), "depth" : 5 * mm});
        }
    });
